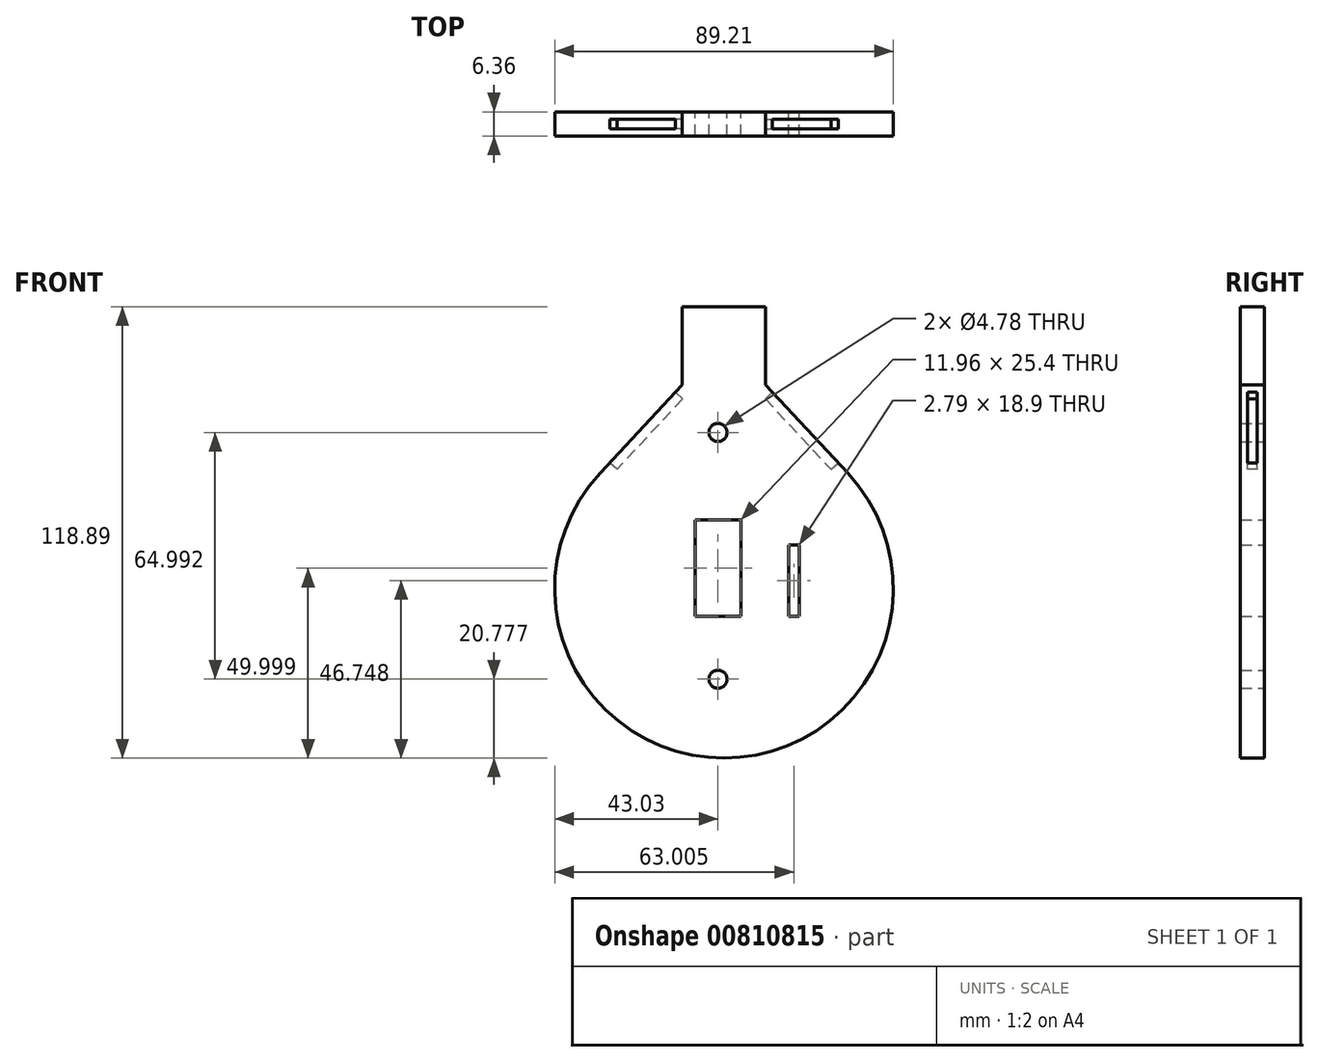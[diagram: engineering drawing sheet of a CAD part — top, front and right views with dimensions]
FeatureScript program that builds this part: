
annotation { "Feature Type Name" : "Feature", "Feature Type Description" : "" }
export const myFeature = defineFeature(function(context is Context, id is Id, definition is map)
    precondition{}
    {
        {
            var Q0;
            Q0=qCreatedBy(makeId("Front.planeOp"),FACE);
            var sketch = newSketch(context, id + "F0", { "sketchPlane" : qUnion([Q0])});
            skArc(sketch, "E0", {"start": v(-31.05, 0) * mm, "mid": v(1.57, -75.03) * mm, "end": v(34.2, 0) * mm});
            skLineSegment(sketch, "E1", {"start": v(-31.05, 0) * mm, "end": v(-9.4, 23.22) * mm});
            skLineSegment(sketch, "E2", {"start": v(34.2, 0) * mm, "end": v(12.55, 23.22) * mm});
            skLineSegment(sketch, "E3", {"start": v(-9.4, 23.22) * mm, "end": v(-9.4, 43.86) * mm});
            skLineSegment(sketch, "E4", {"start": v(12.55, 23.22) * mm, "end": v(12.55, 43.86) * mm});
            skLineSegment(sketch, "E5", {"start": v(-9.4, 43.86) * mm, "end": v(12.55, 43.86) * mm});
            skCircle(sketch, "E6", {"center": v(0, 10.74) * mm, "radius": 2.39 * mm});
            skCircle(sketch, "E7", {"center": v(0, -54.25) * mm, "radius": 2.39 * mm});
            skLineSegment(sketch, "E8.bottom", {"start": v(5.98, -12.33) * mm, "end": v(-5.98, -12.33) * mm});
            skLineSegment(sketch, "E8.top", {"start": v(5.98, -37.73) * mm, "end": v(-5.98, -37.73) * mm});
            skLineSegment(sketch, "E8.left", {"start": v(5.98, -12.33) * mm, "end": v(5.98, -37.73) * mm});
            skLineSegment(sketch, "E8.right", {"start": v(-5.98, -12.33) * mm, "end": v(-5.98, -37.73) * mm});
            skPoint(sketch, "E8.middle", {"position": v(0, -25.03) * mm});
            skLineSegment(sketch, "E9.bottom", {"start": v(18.58, -18.83) * mm, "end": v(21.37, -18.83) * mm});
            skLineSegment(sketch, "E9.top", {"start": v(18.58, -37.73) * mm, "end": v(21.37, -37.73) * mm});
            skLineSegment(sketch, "E9.left", {"start": v(18.58, -18.83) * mm, "end": v(18.58, -37.73) * mm});
            skLineSegment(sketch, "E9.right", {"start": v(21.37, -18.83) * mm, "end": v(21.37, -37.73) * mm});
            skSolve(sketch);
        }
        {
            var Q0;
            Q0=makeQuery(id+"F0.imprint","IMPRINT",FACE,{"disambiguationData":[TD([[makeQuery(id+"F0.imprint","IMPRINT",EDGE,{"derivedFrom":sQuery(id+"F0.wireOp",EDGE,"E0")}),1.0]])]});
            extrude(context, id + "F1", {"entities" : qUnion([Q0]), "endBound" : BoundingType.SYMMETRIC, "depth" : 6.35 * mm, "offsetDistance" : 25.4 * mm});
        }
        {
            var Q0;
            Q0=makeQuery(id+"F1.opExtrude","SWEPT_FACE",FACE,{"disambiguationData":[OSD([sQuery(id+"F0.wireOp",EDGE,"E1")])]});
            cPlane(context, id + "F2", {"entities" : qUnion([Q0]), "cplaneType" : CPlaneType.OFFSET, "offset" : 0 * mm, "width" : 152.4 * mm, "height" : 152.4 * mm});
        }
        {
            var Q0;
            Q0=qCreatedBy(id+"F2.planeOp",FACE);
            var sketch = newSketch(context, id + "F3", { "sketchPlane" : qUnion([Q0])});
            skLineSegment(sketch, "E10.bottom", {"start": v(-1.27, 7.97) * mm, "end": v(1.27, 7.97) * mm});
            skLineSegment(sketch, "E10.top", {"start": v(-1.27, -17.43) * mm, "end": v(1.27, -17.43) * mm});
            skLineSegment(sketch, "E10.left", {"start": v(-1.27, 7.97) * mm, "end": v(-1.27, -17.43) * mm});
            skLineSegment(sketch, "E10.right", {"start": v(1.27, 7.97) * mm, "end": v(1.27, -17.43) * mm});
            skPoint(sketch, "E10.middle", {"position": v(0, -4.73) * mm});
            skSolve(sketch);
        }
        {
            var Q0;
            Q0=makeQuery(id+"F3.imprint","IMPRINT",FACE,{"disambiguationData":[TD([[makeQuery(id+"F3.imprint","IMPRINT",EDGE,{"derivedFrom":sQuery(id+"F3.wireOp",EDGE,"E10.bottom")}),-1.0]])]});
            extrude(context, id + "F4", {"entities" : qUnion([Q0]), "operationType" : NewBodyOperationType.REMOVE, "oppositeDirection" : true, "depth" : 2.54 * mm, "offsetDistance" : 25.4 * mm});
        }
        {
            var Q0;
            Q0=makeQuery(id+"F1.opExtrude","SWEPT_FACE",FACE,{"disambiguationData":[OSD([sQuery(id+"F0.wireOp",EDGE,"E2")])]});
            cPlane(context, id + "F5", {"entities" : qUnion([Q0]), "cplaneType" : CPlaneType.OFFSET, "offset" : 0 * mm, "width" : 152.4 * mm, "height" : 152.4 * mm});
        }
        {
            var Q0;
            Q0=qCreatedBy(id+"F5.planeOp",FACE);
            var sketch = newSketch(context, id + "F6", { "sketchPlane" : qUnion([Q0])});
            skLineSegment(sketch, "E11.bottom", {"start": v(-1.27, 5.82) * mm, "end": v(1.27, 5.82) * mm});
            skLineSegment(sketch, "E11.top", {"start": v(-1.27, -19.58) * mm, "end": v(1.27, -19.58) * mm});
            skLineSegment(sketch, "E11.left", {"start": v(-1.27, 5.82) * mm, "end": v(-1.27, -19.58) * mm});
            skLineSegment(sketch, "E11.right", {"start": v(1.27, 5.82) * mm, "end": v(1.27, -19.58) * mm});
            skPoint(sketch, "E11.middle", {"position": v(0, -6.88) * mm});
            skSolve(sketch);
        }
        {
            var Q0;
            Q0=makeQuery(id+"F6.imprint","IMPRINT",FACE,{"disambiguationData":[TD([[makeQuery(id+"F6.imprint","IMPRINT",EDGE,{"derivedFrom":sQuery(id+"F6.wireOp",EDGE,"E11.bottom")}),-1.0]])]});
            extrude(context, id + "F7", {"entities" : qUnion([Q0]), "operationType" : NewBodyOperationType.REMOVE, "oppositeDirection" : true, "depth" : 2.54 * mm, "offsetDistance" : 25.4 * mm});
        }
    });
